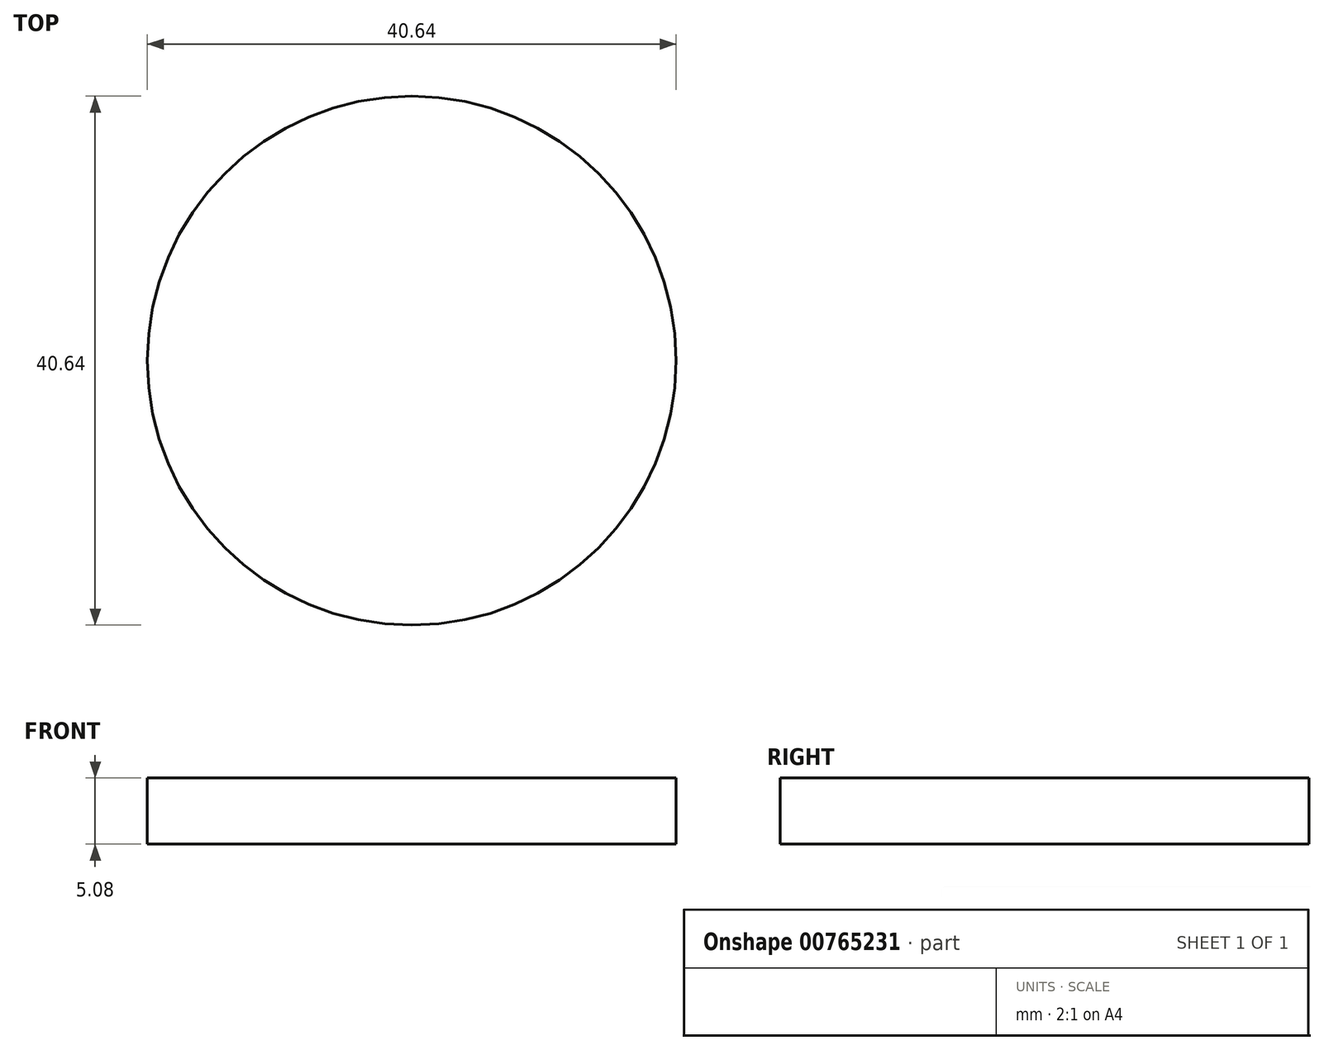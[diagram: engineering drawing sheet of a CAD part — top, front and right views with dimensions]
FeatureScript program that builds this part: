
annotation { "Feature Type Name" : "Feature", "Feature Type Description" : "" }
export const myFeature = defineFeature(function(context is Context, id is Id, definition is map)
    precondition{}
    {
        {
            var Q0;
            Q0=qCreatedBy(makeId("Top.planeOp"),FACE);
            var sketch = newSketch(context, id + "F0", { "sketchPlane" : qUnion([Q0])});
            skCircle(sketch, "E0", {"center": v(0, 0) * mm, "radius": 20.32 * mm});
            skSolve(sketch);
        }
        {
            var Q0;
            Q0 = qSketchRegion(id + "F0", true);
            extrude(context, id + "F1", {"entities" : qUnion([Q0]), "depth" : 5.08 * mm, "offsetDistance" : 25.4 * mm});
        }
    });
